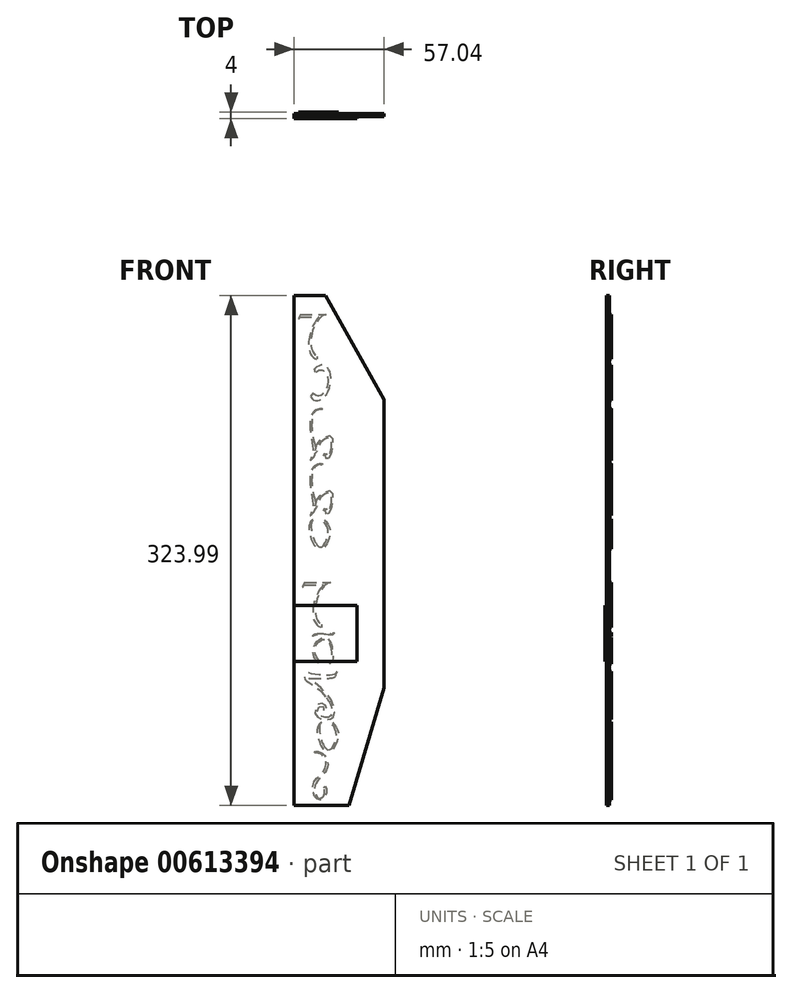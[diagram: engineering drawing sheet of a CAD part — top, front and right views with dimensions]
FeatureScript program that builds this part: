
annotation { "Feature Type Name" : "Feature", "Feature Type Description" : "" }
export const myFeature = defineFeature(function(context is Context, id is Id, definition is map)
    precondition{}
    {
        {
            var Q0;
            Q0=qCreatedBy(makeId("Front.planeOp"),FACE);
            var sketch = newSketch(context, id + "F0", { "sketchPlane" : qUnion([Q0])});
            skLineSegment(sketch, "E0", {"start": v(0, 0) * mm, "end": v(40, 0) * mm});
            skLineSegment(sketch, "E1", {"start": v(40, 0) * mm, "end": v(57.04, 0) * mm});
            skLineSegment(sketch, "E2", {"start": v(57.04, 0) * mm, "end": v(57.04, 166.67) * mm});
            skLineSegment(sketch, "E3", {"start": v(0, 200) * mm, "end": v(0, 0) * mm});
            skLineSegment(sketch, "E4", {"start": v(57.04, 166.67) * mm, "end": v(19.79, 232.6) * mm});
            skPoint(sketch, "E5.center.orphan", {"position": v(28.52, 183.33) * mm});
            skLineSegment(sketch, "E6", {"start": v(19.79, 232.6) * mm, "end": v(0, 232.6) * mm});
            skLineSegment(sketch, "E7", {"start": v(0, 232.6) * mm, "end": v(0, 200) * mm});
            skLineSegment(sketch, "E8", {"start": v(57.04, 0) * mm, "end": v(57.04, -16.7) * mm});
            skLineSegment(sketch, "E9", {"start": v(34.85, -91.4) * mm, "end": v(0, -91.4) * mm});
            skLineSegment(sketch, "E10", {"start": v(0, -91.4) * mm, "end": v(0, 0) * mm});
            skLineSegment(sketch, "E11", {"start": v(34.85, -91.4) * mm, "end": v(57.04, -16.7) * mm});
            skSolve(sketch);
        }
        {
            var Q0;
            Q0=makeQuery(id+"F0.imprint","IMPRINT",FACE,{"disambiguationData":[TD([[makeQuery(id+"F0.imprint","IMPRINT",EDGE,{"derivedFrom":sQuery(id+"F0.wireOp",EDGE,"E0")}),1.0]])]});
            var Q1;
            Q1=makeQuery(id+"F0.imprint","IMPRINT",FACE,{"disambiguationData":[TD([[makeQuery(id+"F0.imprint","IMPRINT",EDGE,{"derivedFrom":sQuery(id+"F0.wireOp",EDGE,"E0")}),-1.0]])]});
            extrude(context, id + "F1", {"entities" : qUnion([Q0, Q1]), "depth" : 2 * mm, "offsetDistance" : 25 * mm});
        }
        {
            var Q0;
            Q0=makeQuery(id+"F1.opExtrude","CAP_FACE",FACE,{"disambiguationData":[OSD([sQuery(id+"F0.wireOp",EDGE,"E0"),sQuery(id+"F0.wireOp",EDGE,"E1"),sQuery(id+"F0.wireOp",EDGE,"E2"),sQuery(id+"F0.wireOp",EDGE,"E3"),sQuery(id+"F0.wireOp",EDGE,"E4"),sQuery(id+"F0.wireOp",EDGE,"E6"),sQuery(id+"F0.wireOp",EDGE,"E7")])],"isStart":true});
            var sketch = newSketch(context, id + "F2", { "sketchPlane" : qUnion([Q0])});
            skLineSegment(sketch, "E12.bottom", {"start": v(-40, 0) * mm, "end": v(0, 0) * mm});
            skLineSegment(sketch, "E12.top", {"start": v(-40, 35.71) * mm, "end": v(0, 35.71) * mm});
            skLineSegment(sketch, "E12.left", {"start": v(-40, 0) * mm, "end": v(-40, 35.71) * mm});
            skLineSegment(sketch, "E12.right", {"start": v(0, 0) * mm, "end": v(0, 35.71) * mm});
            skSolve(sketch);
        }
        {
            var Q0;
            Q0=makeQuery(id+"F2.imprint","IMPRINT",FACE,{"disambiguationData":[TD([[makeQuery(id+"F2.imprint","IMPRINT",EDGE,{"derivedFrom":sQuery(id+"F2.wireOp",EDGE,"E12.bottom")}),1.0]])]});
            extrude(context, id + "F3", {"entities" : qUnion([Q0]), "operationType" : NewBodyOperationType.ADD, "oppositeDirection" : true, "depth" : 3 * mm, "offsetDistance" : 25 * mm});
        }
        {
            var Q0;
            Q0=makeQuery(id+"F1.opExtrude","CAP_FACE",FACE,{"disambiguationData":[OSD([sQuery(id+"F0.wireOp",EDGE,"E2"),sQuery(id+"F0.wireOp",EDGE,"E3"),sQuery(id+"F0.wireOp",EDGE,"E4"),sQuery(id+"F0.wireOp",EDGE,"E6"),sQuery(id+"F0.wireOp",EDGE,"E7"),sQuery(id+"F0.wireOp",EDGE,"E8"),sQuery(id+"F0.wireOp",EDGE,"E9"),sQuery(id+"F0.wireOp",EDGE,"E10"),sQuery(id+"F0.wireOp",EDGE,"E11")])],"isStart":true});
            var sketch = newSketch(context, id + "F4", { "sketchPlane" : qUnion([Q0])});
            skLineSegment(sketch, "E13", {"start": v(3.86, 220.53) * mm, "end": v(7.1, 220.53) * mm});
            skLineSegment(sketch, "E14", {"start": v(3.86, 220.53) * mm, "end": v(2.57, 217.83) * mm});
            skLineSegment(sketch, "E15", {"start": v(2.57, 217.83) * mm, "end": v(2.95, 217.65) * mm});
            skLineSegment(sketch, "E16", {"start": v(2.95, 217.65) * mm, "end": v(3.53, 218.87) * mm});
            skLineSegment(sketch, "E17", {"start": v(3.53, 218.87) * mm, "end": v(15.74, 218.87) * mm});
            skEllipticalArc(sketch, "E18", {});
            skEllipticalArc(sketch, "E19", {});
            skLineSegment(sketch, "E20", {"start": v(7.1, 220.53) * mm, "end": v(20.2, 220.53) * mm});
            skLineSegment(sketch, "E21", {"start": v(14.85, 192.12) * mm, "end": v(14.85, 193.83) * mm});
            skEllipticalArc(sketch, "E22", {});
            skEllipticalArc(sketch, "E23", {});
            skLineSegment(sketch, "E24", {"start": v(13.62, 183.6) * mm, "end": v(12.94, 185.8) * mm});
            skLineSegment(sketch, "E25", {"start": v(11.98, 170.7) * mm, "end": v(10.28, 168.38) * mm});
            skFitSpline(sketch, "E26", {"points": [v(16.98, 160.68) * mm, v(13.52, 159.57) * mm, v(11.18, 157.11) * mm, v(10.06, 148.08) * mm, v(11.85, 134.58) * mm, v(10.17, 127.77) * mm], "startDerivative": vector(-25.24, -6.07) * mm, "endDerivative": vector(-12.16, -30.27) * mm});
            skFitSpline(sketch, "E27", {"points": [v(10.17, 127.77) * mm, v(12.3, 129.8) * mm, v(13.3, 132.12) * mm, v(15.2, 139.15) * mm, v(19.55, 142.39) * mm, v(23.45, 143.4) * mm, v(23.67, 133.13) * mm, v(21, 128.66) * mm, v(18.68, 129.12) * mm, v(18.74, 131.71) * mm, v(20.8, 132.38) * mm, v(20.4, 131.51) * mm, v(19.54, 131.25) * mm, v(19.87, 129.2) * mm, v(21.23, 129.27) * mm, v(23.12, 133.02) * mm, v(23.12, 141.9) * mm, v(20.5, 141.9) * mm, v(16.18, 138.62) * mm, v(14.14, 133.1) * mm], "startDerivative": vector(50.8, 43.85) * mm, "endDerivative": vector(-20, -100.63) * mm});
            skFitSpline(sketch, "E28", {"points": [v(14.14, 133.1) * mm, v(13.3, 132.12) * mm], "startDerivative": vector(-0.84, -0.98) * mm, "endDerivative": vector(-0.84, -0.98) * mm});
            skFitSpline(sketch, "E29", {"points": [v(16.98, 160.68) * mm, v(17.97, 160.68) * mm, v(17.57, 160.04) * mm, v(16.7, 160.14) * mm, v(13.9, 159.27) * mm, v(12.1, 157.11) * mm, v(11.18, 148.08) * mm, v(13.3, 136.6) * mm, v(13.66, 134.03) * mm], "startDerivative": vector(19.65, 3.96) * mm, "endDerivative": vector(1.63, -18.4) * mm});
            skFitSpline(sketch, "E30", {"points": [v(16.98, 125.68) * mm, v(13.52, 124.57) * mm, v(11.18, 122.11) * mm, v(10.06, 113.08) * mm, v(11.85, 99.58) * mm, v(10.17, 92.77) * mm], "startDerivative": vector(-25.24, -6.07) * mm, "endDerivative": vector(-12.16, -30.27) * mm});
            skFitSpline(sketch, "E31", {"points": [v(10.17, 92.77) * mm, v(12.3, 94.8) * mm, v(13.3, 97.12) * mm, v(15.2, 104.15) * mm, v(19.55, 107.39) * mm, v(23.45, 108.4) * mm, v(23.67, 98.13) * mm, v(21, 93.66) * mm, v(18.68, 94.12) * mm, v(18.74, 96.71) * mm, v(20.8, 97.38) * mm, v(20.4, 96.51) * mm, v(19.54, 96.25) * mm, v(19.87, 94.2) * mm, v(21.23, 94.27) * mm, v(23.12, 98.02) * mm, v(23.12, 106.9) * mm, v(20.5, 106.9) * mm, v(16.18, 103.62) * mm, v(14.14, 98.1) * mm], "startDerivative": vector(50.8, 43.85) * mm, "endDerivative": vector(-20, -100.63) * mm});
            skFitSpline(sketch, "E32", {"points": [v(14.14, 98.1) * mm, v(13.3, 97.12) * mm], "startDerivative": vector(-0.84, -0.98) * mm, "endDerivative": vector(-0.84, -0.98) * mm});
            skFitSpline(sketch, "E33", {"points": [v(16.98, 125.68) * mm, v(17.97, 125.68) * mm, v(17.57, 125.04) * mm, v(16.7, 125.14) * mm, v(13.9, 124.27) * mm, v(12.1, 122.11) * mm, v(11.18, 113.08) * mm, v(13.3, 101.6) * mm, v(13.66, 99.03) * mm], "startDerivative": vector(19.65, 3.96) * mm, "endDerivative": vector(1.63, -18.4) * mm});
            skFitSpline(sketch, "E34", {"points": [v(12.01, 90.1) * mm, v(10.84, 87.57) * mm, v(12.7, 77.09) * mm, v(16.05, 72.72) * mm], "startDerivative": vector(-6.54, -8.17) * mm, "endDerivative": vector(11.14, -10.32) * mm});
            skFitSpline(sketch, "E35", {"points": [v(12.01, 90.1) * mm, v(10.84, 89.48) * mm, v(9.9, 87.57) * mm, v(9.38, 84.05) * mm, v(12.7, 73.94) * mm, v(15.88, 71.56) * mm], "startDerivative": vector(-10.77, -3.6) * mm, "endDerivative": vector(15.89, -6.97) * mm});
            skFitSpline(sketch, "E36", {"points": [v(16.05, 72.72) * mm, v(18.2, 73.3) * mm, v(19.78, 75.83) * mm, v(21.47, 81.19) * mm, v(20.86, 85.67) * mm, v(19.09, 88.5) * mm, v(17.5, 90.1) * mm, v(18.25, 90.66) * mm, v(19.73, 89.48) * mm, v(22.25, 85.7) * mm, v(22.7, 80.87) * mm, v(19.15, 72.72) * mm, v(15.88, 71.56) * mm], "startDerivative": vector(35.6, 3.82) * mm, "endDerivative": vector(-40.74, -3.34) * mm});
            skLineSegment(sketch, "E37", {"start": v(6.62, 50.23) * mm, "end": v(9.84, 50.23) * mm});
            skLineSegment(sketch, "E38", {"start": v(6.62, 50.23) * mm, "end": v(5.32, 47.54) * mm});
            skLineSegment(sketch, "E39", {"start": v(5.32, 47.54) * mm, "end": v(5.7, 47.36) * mm});
            skLineSegment(sketch, "E40", {"start": v(5.7, 47.36) * mm, "end": v(6.29, 48.57) * mm});
            skLineSegment(sketch, "E41", {"start": v(6.29, 48.57) * mm, "end": v(18.5, 48.57) * mm});
            skEllipticalArc(sketch, "E42", {});
            skEllipticalArc(sketch, "E43", {});
            skLineSegment(sketch, "E44", {"start": v(9.84, 50.23) * mm, "end": v(22.95, 50.23) * mm});
            skLineSegment(sketch, "E45", {"start": v(17.6, 21.82) * mm, "end": v(17.6, 23.54) * mm});
            skFitSpline(sketch, "E46", {"points": [v(15, -0.86) * mm, v(13.02, 2.13) * mm, v(11.87, 6.75) * mm, v(13.24, 11.32) * mm, v(18.87, 15.3) * mm, v(23.06, 12.43) * mm, v(24.3, 5.5) * mm, v(24.36, 1.07) * mm, v(22.4, -1.35) * mm], "startDerivative": vector(-19.8, 25.5) * mm, "endDerivative": vector(-24.34, -21.8) * mm});
            skFitSpline(sketch, "E47", {"points": [v(15, -0.86) * mm, v(15.51, 0.65) * mm, v(14.29, 2.7) * mm, v(13.02, 6.63) * mm, v(14.29, 11) * mm, v(18.86, 14.22) * mm, v(22.16, 11.89) * mm, v(23.62, 5.59) * mm, v(23.68, 1.3) * mm, v(22.4, -1.35) * mm], "startDerivative": vector(12.33, 21.15) * mm, "endDerivative": vector(-16.23, -25.62) * mm});
            skFitSpline(sketch, "E48", {"points": [v(11.67, 16.35) * mm, v(12.3, 17.03) * mm, v(13.71, 17.64) * mm, v(22.93, 17.91) * mm], "startDerivative": vector(3.18, 3.9) * mm, "endDerivative": vector(19.32, -0.2) * mm});
            skFitSpline(sketch, "E49", {"points": [v(22.93, 17.91) * mm, v(23.8, 17.37) * mm, v(24.93, 17.91) * mm, v(25, 18.57) * mm], "startDerivative": vector(2.24, -2.27) * mm, "endDerivative": vector(-0.34, 2.4) * mm});
            skFitSpline(sketch, "E50", {"points": [v(25, 18.57) * mm, v(25.26, 18.3) * mm, v(25.18, 17.84) * mm, v(24.53, 17.21) * mm, v(23.5, 16.97) * mm, v(22.4, 17.06) * mm, v(13.57, 16.88) * mm, v(12.8, 16.6) * mm, v(12.33, 16.41) * mm, v(11.59, 15.96) * mm], "startDerivative": vector(5.2, -3.62) * mm, "endDerivative": vector(-8.06, -5.5) * mm});
            skFitSpline(sketch, "E51", {"points": [v(11.67, 16.35) * mm, v(11.59, 15.96) * mm], "startDerivative": vector(-0.08, -0.4) * mm, "endDerivative": vector(-0.08, -0.4) * mm});
            skFitSpline(sketch, "E52", {"points": [v(27.09, -6.15) * mm, v(25.65, -7.96) * mm, v(22, -8.61) * mm, v(12.36, -8.02) * mm, v(7.91, -7.46) * mm, v(6.49, -10.7) * mm, v(9.7, -13.3) * mm, v(15.49, -17.53) * mm, v(20.5, -22.94) * mm], "startDerivative": vector(-13.85, -20.96) * mm, "endDerivative": vector(50.43, -64.75) * mm});
            skFitSpline(sketch, "E53", {"points": [v(20.5, -22.94) * mm, v(23.39, -28.15) * mm, v(23.23, -34.3) * mm, v(18.02, -35.1) * mm, v(14.7, -31.15) * mm], "startDerivative": vector(11.95, -17.68) * mm, "endDerivative": vector(8.08, 21.68) * mm});
            skFitSpline(sketch, "E54", {"points": [v(14.7, -31.15) * mm, v(16.29, -28.46) * mm, v(18.97, -29.25) * mm, v(18.31, -31.15) * mm, v(19.06, -32.21) * mm, v(19.81, -31.15) * mm, v(20.56, -29.02) * mm, v(18.87, -26.96) * mm, v(15.4, -26.77) * mm, v(13.15, -31.15) * mm, v(14.7, -35.12) * mm, v(18.02, -36.53) * mm, v(23.1, -36.43) * mm, v(24.88, -35.1) * mm, v(24.97, -28.08) * mm, v(19.25, -18.89) * mm, v(9.4, -10.54) * mm], "startDerivative": vector(15.98, 63.28) * mm, "endDerivative": vector(-91.6, 70.25) * mm});
            skFitSpline(sketch, "E55", {"points": [v(9.4, -10.54) * mm, v(21.97, -10.54) * mm, v(25.82, -9.5) * mm, v(27.09, -6.15) * mm], "startDerivative": vector(29.6, -0.49) * mm, "endDerivative": vector(3.16, 15.37) * mm});
            skFitSpline(sketch, "E56", {"points": [v(17.21, -38.69) * mm, v(16.04, -41.22) * mm, v(17.9, -51.7) * mm, v(21.25, -56.07) * mm], "startDerivative": vector(-6.54, -8.17) * mm, "endDerivative": vector(11.14, -10.32) * mm});
            skFitSpline(sketch, "E57", {"points": [v(17.21, -38.69) * mm, v(16.04, -39.31) * mm, v(15.1, -41.22) * mm, v(14.58, -44.74) * mm, v(17.9, -54.85) * mm, v(21.08, -57.24) * mm], "startDerivative": vector(-10.77, -3.6) * mm, "endDerivative": vector(15.89, -6.97) * mm});
            skFitSpline(sketch, "E58", {"points": [v(21.25, -56.07) * mm, v(23.4, -55.49) * mm, v(24.98, -52.96) * mm, v(26.67, -47.6) * mm, v(26.06, -43.12) * mm, v(24.29, -40.3) * mm, v(22.7, -38.69) * mm, v(23.45, -38.13) * mm, v(24.93, -39.31) * mm, v(27.45, -43.1) * mm, v(27.9, -47.92) * mm, v(24.35, -56.07) * mm, v(21.08, -57.24) * mm], "startDerivative": vector(35.6, 3.82) * mm, "endDerivative": vector(-40.74, -3.34) * mm});
            skFitSpline(sketch, "E59", {"points": [v(13.66, -56.9) * mm, v(17.04, -57.74) * mm, v(19.76, -60.09) * mm, v(21.17, -63.28) * mm, v(21.08, -66.94) * mm, v(18.82, -71.35) * mm, v(15.54, -74.82) * mm, v(13.66, -77.82) * mm, v(12.82, -81.95) * mm, v(13.94, -84.86) * mm, v(15.92, -87.02) * mm], "startDerivative": vector(36.83, -5.4) * mm, "endDerivative": vector(51.01, -25.5) * mm});
            skFitSpline(sketch, "E60", {"points": [v(15.92, -87.02) * mm, v(18.07, -86.17) * mm, v(19.1, -83.92) * mm, v(19.2, -80.73) * mm, v(18.45, -80.07) * mm], "startDerivative": vector(9.38, 2.2) * mm, "endDerivative": vector(-5.22, 2.52) * mm});
            skFitSpline(sketch, "E61", {"points": [v(18.45, -80.07) * mm, v(19.5, -79.32) * mm, v(20.37, -80.21) * mm, v(20.21, -84.3) * mm, v(18.74, -87.02) * mm, v(16.9, -87.92) * mm, v(13.98, -87.02) * mm, v(12.4, -84.3) * mm, v(11.7, -81.95) * mm, v(12, -77.98) * mm, v(14.14, -74.35) * mm, v(17.61, -70.8) * mm, v(20.06, -66.86) * mm, v(20.14, -63.15) * mm, v(18.74, -60.07) * mm, v(15.92, -58.34) * mm, v(12.8, -57.86) * mm, v(13.66, -56.9) * mm], "startDerivative": vector(27, 28.36) * mm, "endDerivative": vector(-10.77, 30.94) * mm});
            skLineSegment(sketch, "E62", {"start": v(0, -76.84) * mm, "end": v(0, -91.4) * mm});
            skLineSegment(sketch, "E63", {"start": v(0, -91.4) * mm, "end": v(8.12, -91.4) * mm});
            const initialGuessF4  = {"E18": [0.01854486947105799, 0.20709701367466082, 0.3140856699790382, 0.9493946449784825, 0.015537334011104582, 0.008485907113070932, 0.6388991419615135, 3.2831460951122207], "E19": [0.01854486947105799, 0.20709701367466082, 0.24253552143487014, 0.9701425260456917, 0.013780557752704876, 0.007388543269675694, 0.2259031223263688, 3.0918384497159126], "E22": [0.016064272787156386, 0.177044040717169, 0.2313512452415796, 0.9728702900824809, 0.011468486584754524, 0.006902209779284208, 2.5896167459862616, 0.8233252755202497], "E23": [0.016064272787156386, 0.177044040717169, 0.21490751269293634, 0.9766344049787186, 0.008016117309888379, 0.005600430553553324, 2.65407990850102, 0.7464193260421231], "E42": [0.021298223862533633, 0.03680388277507052, 0.3140856699790382, 0.9493946449784825, 0.015537334011104582, 0.008485907113070932, 0.6388991419615135, 3.2831460951122207], "E43": [0.021298223862533633, 0.03680388277507052, 0.24253552143487014, 0.9701425260456917, 0.013780557752704876, 0.007388543269675694, 0.2259031223263688, 3.0918384497159126]};
            skSetInitialGuess(sketch, initialGuessF4);
            skSolve(sketch);
        }
        {
            var Q0;
            Q0 = qSketchRegion(id + "F4", true);
            var Q1;
            Q1 = qConstructionFilter(qBodyType(qCreatedBy(id + "F4" ,EDGE), BodyType.WIRE), ConstructionObject.NO);
            extrude(context, id + "F5", {"entities" : qUnion([Q0]), "surfaceEntities" : qUnion([Q1]), "depth" : 1 * mm, "offsetDistance" : 25 * mm});
        }
        {
            var Q0;
            Q0=makeQuery(id+"F5.opExtrude","SWEPT_BODY",BODY,{"disambiguationData":[OSD([sQuery(id+"F4.wireOp",EDGE,"E13"),sQuery(id+"F4.wireOp",EDGE,"E14"),sQuery(id+"F4.wireOp",EDGE,"E15"),sQuery(id+"F4.wireOp",EDGE,"E16"),sQuery(id+"F4.wireOp",EDGE,"E17"),sQuery(id+"F4.wireOp",EDGE,"E18"),sQuery(id+"F4.wireOp",EDGE,"E19"),sQuery(id+"F4.wireOp",EDGE,"E20"),sQuery(id+"F4.wireOp",EDGE,"E21")])]});
            var Q1;
            Q1=makeQuery(id+"F5.opExtrude","SWEPT_BODY",BODY,{"disambiguationData":[OSD([sQuery(id+"F4.wireOp",EDGE,"E22"),sQuery(id+"F4.wireOp",EDGE,"E23"),sQuery(id+"F4.wireOp",EDGE,"E24"),sQuery(id+"F4.wireOp",EDGE,"E25")])]});
            var Q2;
            Q2=makeQuery(id+"F5.opExtrude","SWEPT_BODY",BODY,{"disambiguationData":[OSD([sQuery(id+"F4.wireOp",EDGE,"E26"),sQuery(id+"F4.wireOp",EDGE,"E27"),sQuery(id+"F4.wireOp",EDGE,"E28"),sQuery(id+"F4.wireOp",EDGE,"E29")])]});
            var Q3;
            Q3=makeQuery(id+"F5.opExtrude","SWEPT_BODY",BODY,{"disambiguationData":[OSD([sQuery(id+"F4.wireOp",EDGE,"E30"),sQuery(id+"F4.wireOp",EDGE,"E31"),sQuery(id+"F4.wireOp",EDGE,"E32"),sQuery(id+"F4.wireOp",EDGE,"E33")])]});
            var Q4;
            Q4=makeQuery(id+"F5.opExtrude","SWEPT_BODY",BODY,{"disambiguationData":[OSD([sQuery(id+"F4.wireOp",EDGE,"E34"),sQuery(id+"F4.wireOp",EDGE,"E35"),sQuery(id+"F4.wireOp",EDGE,"E36")])]});
            var Q5;
            Q5=makeQuery(id+"F5.opExtrude","SWEPT_BODY",BODY,{"disambiguationData":[OSD([sQuery(id+"F4.wireOp",EDGE,"E37"),sQuery(id+"F4.wireOp",EDGE,"E38"),sQuery(id+"F4.wireOp",EDGE,"E39"),sQuery(id+"F4.wireOp",EDGE,"E40"),sQuery(id+"F4.wireOp",EDGE,"E41"),sQuery(id+"F4.wireOp",EDGE,"E42"),sQuery(id+"F4.wireOp",EDGE,"E43"),sQuery(id+"F4.wireOp",EDGE,"E44"),sQuery(id+"F4.wireOp",EDGE,"E45")])]});
            var Q6;
            Q6=makeQuery(id+"F5.opExtrude","SWEPT_BODY",BODY,{"disambiguationData":[OSD([sQuery(id+"F4.wireOp",EDGE,"E46"),sQuery(id+"F4.wireOp",EDGE,"E47")])]});
            var Q7;
            Q7=makeQuery(id+"F5.opExtrude","SWEPT_BODY",BODY,{"disambiguationData":[OSD([sQuery(id+"F4.wireOp",EDGE,"E48"),sQuery(id+"F4.wireOp",EDGE,"E49"),sQuery(id+"F4.wireOp",EDGE,"E50"),sQuery(id+"F4.wireOp",EDGE,"E51")])]});
            var Q8;
            Q8=makeQuery(id+"F5.opExtrude","SWEPT_BODY",BODY,{"disambiguationData":[OSD([sQuery(id+"F4.wireOp",EDGE,"E52"),sQuery(id+"F4.wireOp",EDGE,"E53"),sQuery(id+"F4.wireOp",EDGE,"E54"),sQuery(id+"F4.wireOp",EDGE,"E55")])]});
            var Q9;
            Q9=makeQuery(id+"F5.opExtrude","SWEPT_BODY",BODY,{"disambiguationData":[OSD([sQuery(id+"F4.wireOp",EDGE,"E56"),sQuery(id+"F4.wireOp",EDGE,"E57"),sQuery(id+"F4.wireOp",EDGE,"E58")])]});
            var Q10;
            Q10=makeQuery(id+"F5.opExtrude","SWEPT_BODY",BODY,{"disambiguationData":[OSD([sQuery(id+"F4.wireOp",EDGE,"E59"),sQuery(id+"F4.wireOp",EDGE,"E60"),sQuery(id+"F4.wireOp",EDGE,"E61")])]});
            var Q11;
            Q11=qCreatedBy(makeId("Right.planeOp"),FACE);
            mirror(context, id + "F6", {"operationType" : NewBodyOperationType.ADD, "entities" : qUnion([Q0, Q1, Q2, Q3, Q4, Q5, Q6, Q7, Q8, Q9, Q10]), "mirrorPlane" : qUnion([Q11])});
        }
        {
            var Q0;
            Q0=makeQuery(id+"F5.opExtrude","SWEPT_BODY",BODY,{"disambiguationData":[OSD([sQuery(id+"F4.wireOp",EDGE,"E46"),sQuery(id+"F4.wireOp",EDGE,"E47")])]});
            deleteBodies(context, id + "F7", {"entities" : qUnion([Q0])});
        }
        {
            var Q0;
            Q0=makeQuery(id+"F5.opExtrude","SWEPT_BODY",BODY,{"disambiguationData":[OSD([sQuery(id+"F4.wireOp",EDGE,"E37"),sQuery(id+"F4.wireOp",EDGE,"E38"),sQuery(id+"F4.wireOp",EDGE,"E39"),sQuery(id+"F4.wireOp",EDGE,"E40"),sQuery(id+"F4.wireOp",EDGE,"E41"),sQuery(id+"F4.wireOp",EDGE,"E42"),sQuery(id+"F4.wireOp",EDGE,"E43"),sQuery(id+"F4.wireOp",EDGE,"E44"),sQuery(id+"F4.wireOp",EDGE,"E45")])]});
            var Q1;
            Q1=makeQuery(id+"F5.opExtrude","SWEPT_BODY",BODY,{"disambiguationData":[OSD([sQuery(id+"F4.wireOp",EDGE,"E48"),sQuery(id+"F4.wireOp",EDGE,"E49"),sQuery(id+"F4.wireOp",EDGE,"E50"),sQuery(id+"F4.wireOp",EDGE,"E51")])]});
            var Q2;
            Q2=makeQuery(id+"F5.opExtrude","SWEPT_BODY",BODY,{"disambiguationData":[OSD([sQuery(id+"F4.wireOp",EDGE,"E13"),sQuery(id+"F4.wireOp",EDGE,"E14"),sQuery(id+"F4.wireOp",EDGE,"E15"),sQuery(id+"F4.wireOp",EDGE,"E16"),sQuery(id+"F4.wireOp",EDGE,"E17"),sQuery(id+"F4.wireOp",EDGE,"E18"),sQuery(id+"F4.wireOp",EDGE,"E19"),sQuery(id+"F4.wireOp",EDGE,"E20"),sQuery(id+"F4.wireOp",EDGE,"E21")])]});
            var Q3;
            Q3=makeQuery(id+"F5.opExtrude","SWEPT_BODY",BODY,{"disambiguationData":[OSD([sQuery(id+"F4.wireOp",EDGE,"E26"),sQuery(id+"F4.wireOp",EDGE,"E27"),sQuery(id+"F4.wireOp",EDGE,"E28"),sQuery(id+"F4.wireOp",EDGE,"E29")])]});
            var Q4;
            Q4=makeQuery(id+"F5.opExtrude","SWEPT_BODY",BODY,{"disambiguationData":[OSD([sQuery(id+"F4.wireOp",EDGE,"E22"),sQuery(id+"F4.wireOp",EDGE,"E23"),sQuery(id+"F4.wireOp",EDGE,"E24"),sQuery(id+"F4.wireOp",EDGE,"E25")])]});
            var Q5;
            Q5=makeQuery(id+"F5.opExtrude","SWEPT_BODY",BODY,{"disambiguationData":[OSD([sQuery(id+"F4.wireOp",EDGE,"E30"),sQuery(id+"F4.wireOp",EDGE,"E31"),sQuery(id+"F4.wireOp",EDGE,"E32"),sQuery(id+"F4.wireOp",EDGE,"E33")])]});
            deleteBodies(context, id + "F8", {"entities" : qUnion([Q0, Q1, Q2, Q3, Q4, Q5])});
        }
        {
            var Q0;
            Q0=makeQuery(id+"F5.opExtrude","SWEPT_BODY",BODY,{"disambiguationData":[OSD([sQuery(id+"F4.wireOp",EDGE,"E34"),sQuery(id+"F4.wireOp",EDGE,"E35"),sQuery(id+"F4.wireOp",EDGE,"E36")])]});
            var Q1;
            Q1=makeQuery(id+"F5.opExtrude","SWEPT_BODY",BODY,{"disambiguationData":[OSD([sQuery(id+"F4.wireOp",EDGE,"E52"),sQuery(id+"F4.wireOp",EDGE,"E53"),sQuery(id+"F4.wireOp",EDGE,"E54"),sQuery(id+"F4.wireOp",EDGE,"E55")])]});
            var Q2;
            Q2=makeQuery(id+"F5.opExtrude","SWEPT_BODY",BODY,{"disambiguationData":[OSD([sQuery(id+"F4.wireOp",EDGE,"E56"),sQuery(id+"F4.wireOp",EDGE,"E57"),sQuery(id+"F4.wireOp",EDGE,"E58")])]});
            var Q3;
            Q3=makeQuery(id+"F5.opExtrude","SWEPT_BODY",BODY,{"disambiguationData":[OSD([sQuery(id+"F4.wireOp",EDGE,"E59"),sQuery(id+"F4.wireOp",EDGE,"E60"),sQuery(id+"F4.wireOp",EDGE,"E61")])]});
            deleteBodies(context, id + "F9", {"entities" : qUnion([Q0, Q1, Q2, Q3])});
        }
    });
